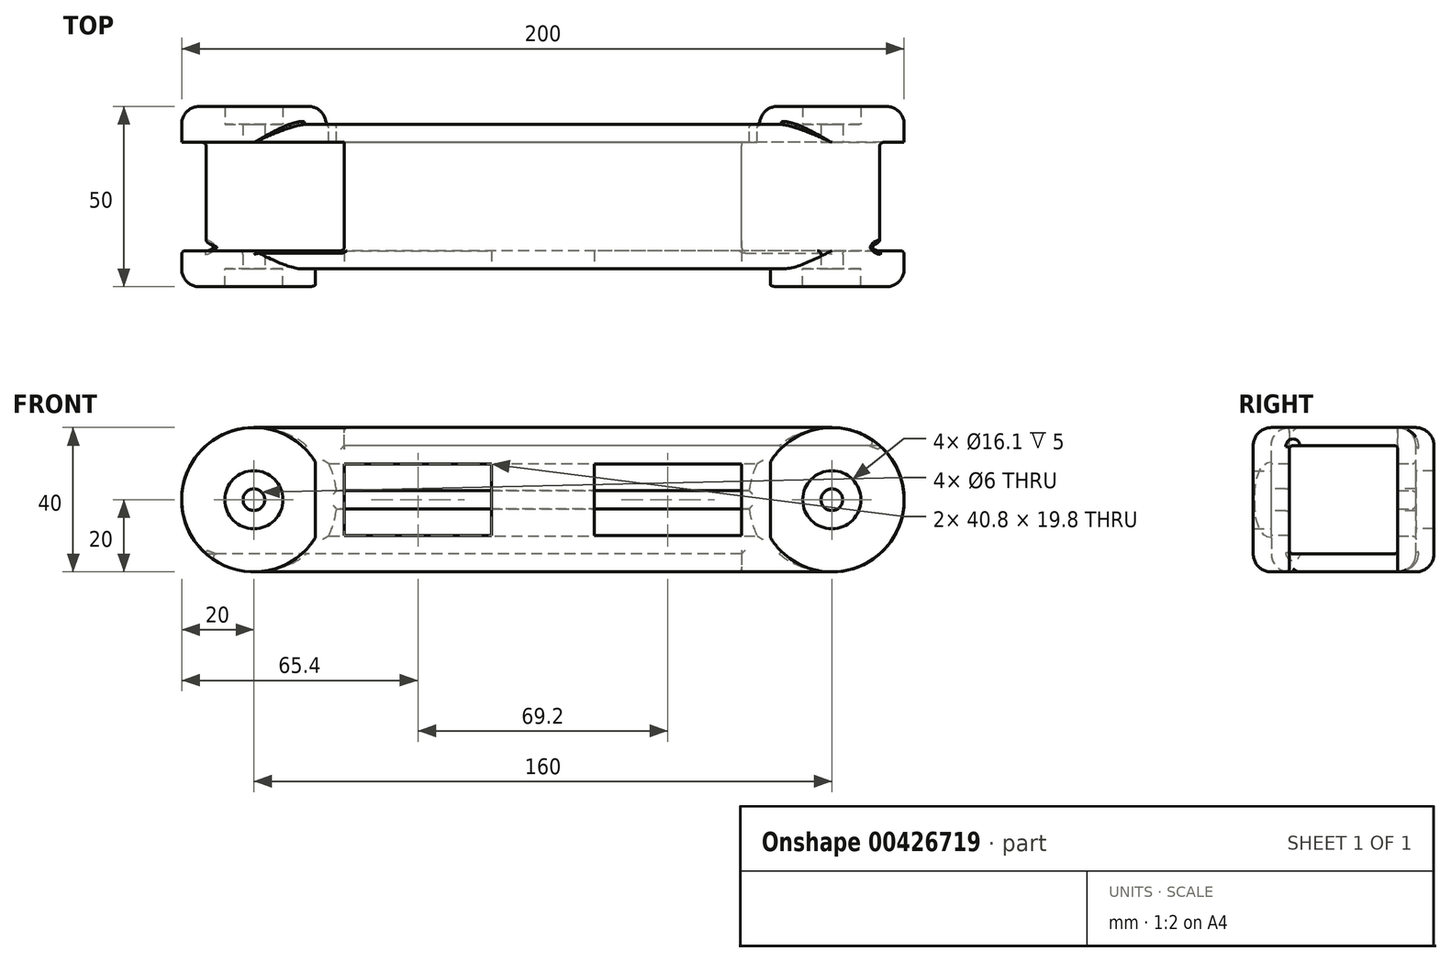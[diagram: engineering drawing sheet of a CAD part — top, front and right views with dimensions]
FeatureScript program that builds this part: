
annotation { "Feature Type Name" : "Feature", "Feature Type Description" : "" }
export const myFeature = defineFeature(function(context is Context, id is Id, definition is map)
    precondition{}
    {
        {
            var Q0;
            Q0=qCreatedBy(makeId("Right.planeOp"),FACE);
            var sketch = newSketch(context, id + "F0", { "sketchPlane" : qUnion([Q0])});
            skLineSegment(sketch, "E0.bottom", {"start": v(-20, -20) * mm, "end": v(20, -20) * mm});
            skLineSegment(sketch, "E0.top", {"start": v(-20, 20) * mm, "end": v(20, 20) * mm});
            skLineSegment(sketch, "E0.left", {"start": v(-20, -20) * mm, "end": v(-20, 20) * mm});
            skLineSegment(sketch, "E0.right", {"start": v(20, -20) * mm, "end": v(20, 20) * mm});
            skPoint(sketch, "E0.middle", {"position": v(0, 0) * mm});
            skLineSegment(sketch, "E1.bottom", {"start": v(-15, -15) * mm, "end": v(15, -15) * mm});
            skLineSegment(sketch, "E1.top", {"start": v(-15, 15) * mm, "end": v(15, 15) * mm});
            skLineSegment(sketch, "E1.left", {"start": v(-15, -15) * mm, "end": v(-15, 15) * mm});
            skLineSegment(sketch, "E1.right", {"start": v(15, -15) * mm, "end": v(15, 15) * mm});
            skSolve(sketch);
        }
        {
            var Q0;
            Q0=makeQuery(id+"F0.imprint","IMPRINT",FACE,{"disambiguationData":[TD([[makeQuery(id+"F0.imprint","IMPRINT",EDGE,{"derivedFrom":sQuery(id+"F0.wireOp",EDGE,"E0.bottom")}),1.0]])]});
            extrude(context, id + "F1", {"entities" : qUnion([Q0]), "depth" : 200 * mm});
        }
        {
            var Q0;
            Q0=makeQuery(id+"F1.opExtrude","SWEPT_FACE",FACE,{"disambiguationData":[OSD([sQuery(id+"F0.wireOp",EDGE,"E0.right")])]});
            var sketch = newSketch(context, id + "F2", { "sketchPlane" : qUnion([Q0])});
            skLineSegment(sketch, "E2", {"start": v(-238.83, 0) * mm, "end": v(24.92, 0) * mm, "construction": true});
            skPoint(sketch, "E2.endSnap0", {"position": v(-200, 0) * mm});
            skCircle(sketch, "E3", {"center": v(-180, 0) * mm, "radius": 20 * mm});
            skCircle(sketch, "E4", {"center": v(-20, 0) * mm, "radius": 20 * mm});
            skSolve(sketch);
        }
        {
            var Q0;
            {var subQ0=sQuery(id+"F2.wireOp",EDGE,"E3");var subQ1=sQuery(id+"F0.wireOp",EDGE,"E0.right");var subQ2=makeQuery(id+"F1.opExtrude","CAP_EDGE",EDGE,{"disambiguationData":[OSD([subQ1])],"isStart":false});var subQ3=makeQuery(id+"F2.imprint","INTERSECT",VERTEX,{"derivedFrom":[subQ2,subQ0]});Q0=makeQuery(id+"F2.imprint","IMPRINT",FACE,{"disambiguationData":[TD([[makeQuery(id+"F2.imprint","IMPRINT",EDGE,{"disambiguationData":[TD([[subQ3,-1.0]])],"derivedFrom":subQ0}),-1.0]])]});}
            var Q1;
            {var subQ0=sQuery(id+"F2.wireOp",EDGE,"E3");var subQ1=sQuery(id+"F0.wireOp",EDGE,"E0.right");var subQ2=makeQuery(id+"F1.opExtrude","CAP_EDGE",EDGE,{"disambiguationData":[OSD([subQ1])],"isStart":false});var subQ3=makeQuery(id+"F2.imprint","INTERSECT",VERTEX,{"derivedFrom":[subQ2,subQ0]});Q1=makeQuery(id+"F2.imprint","IMPRINT",FACE,{"disambiguationData":[TD([[makeQuery(id+"F2.imprint","IMPRINT",EDGE,{"disambiguationData":[TD([[subQ3,1.0]])],"derivedFrom":subQ0}),-1.0]])]});}
            var Q2;
            {var subQ0=sQuery(id+"F2.wireOp",EDGE,"E4");var subQ1=sQuery(id+"F0.wireOp",EDGE,"E0.right");var subQ4=makeQuery(id+"F1.opExtrude","CAP_EDGE",EDGE,{"disambiguationData":[OSD([subQ1])],"isStart":true});var subQ5=makeQuery(id+"F2.imprint","INTERSECT",VERTEX,{"derivedFrom":[subQ4,subQ0]});Q2=makeQuery(id+"F2.imprint","IMPRINT",FACE,{"disambiguationData":[TD([[makeQuery(id+"F2.imprint","IMPRINT",EDGE,{"disambiguationData":[TD([[subQ5,-1.0]])],"derivedFrom":subQ0}),-1.0]])]});}
            var Q3;
            {var subQ0=sQuery(id+"F2.wireOp",EDGE,"E4");var subQ1=sQuery(id+"F0.wireOp",EDGE,"E0.right");var subQ2=makeQuery(id+"F1.opExtrude","CAP_EDGE",EDGE,{"disambiguationData":[OSD([subQ1])],"isStart":true});var subQ3=makeQuery(id+"F2.imprint","INTERSECT",VERTEX,{"derivedFrom":[subQ2,subQ0]});Q3=makeQuery(id+"F2.imprint","IMPRINT",FACE,{"disambiguationData":[TD([[makeQuery(id+"F2.imprint","IMPRINT",EDGE,{"disambiguationData":[TD([[subQ3,1.0]])],"derivedFrom":subQ0}),-1.0]])]});}
            extrude(context, id + "F3", {"entities" : qUnion([Q0, Q1, Q2, Q3]), "operationType" : NewBodyOperationType.REMOVE, "oppositeDirection" : true, "depth" : 40 * mm});
        }
        {
            var Q0;
            Q0=makeQuery(id+"F1.opExtrude","SWEPT_FACE",FACE,{"disambiguationData":[OSD([sQuery(id+"F0.wireOp",EDGE,"E0.right")])]});
            var sketch = newSketch(context, id + "F4", { "sketchPlane" : qUnion([Q0])});
            skLineSegment(sketch, "E5", {"start": v(-227.1, 0) * mm, "end": v(25.36, 0) * mm, "construction": true});
            skCircle(sketch, "E6", {"center": v(-180, 0) * mm, "radius": 20 * mm});
            skCircle(sketch, "E7", {"center": v(-20, 0) * mm, "radius": 20 * mm});
            skCircle(sketch, "E8", {"center": v(-20, 0) * mm, "radius": 8.05 * mm});
            skCircle(sketch, "E9", {"center": v(-180, 0) * mm, "radius": 8.05 * mm});
            skSolve(sketch);
        }
        {
            var Q0;
            Q0 = qSketchRegion(id + "F4", true);
            extrude(context, id + "F5", {"entities" : qUnion([Q0]), "operationType" : NewBodyOperationType.ADD, "depth" : 5 * mm});
        }
        {
            var Q0;
            Q0=makeQuery(id+"F1.opExtrude","SWEPT_FACE",FACE,{"disambiguationData":[OSD([sQuery(id+"F0.wireOp",EDGE,"E0.left")])]});
            var sketch = newSketch(context, id + "F6", { "sketchPlane" : qUnion([Q0])});
            skLineSegment(sketch, "E10", {"start": v(-11.87, 0) * mm, "end": v(168.62, 0) * mm, "construction": true});
            skCircle(sketch, "E11", {"center": v(20, 0) * mm, "radius": 20 * mm});
            skCircle(sketch, "E12", {"center": v(20, 0) * mm, "radius": 8.05 * mm});
            skCircle(sketch, "E13", {"center": v(180, 0) * mm, "radius": 20 * mm});
            skCircle(sketch, "E14", {"center": v(180, 0) * mm, "radius": 8.05 * mm});
            skSolve(sketch);
        }
        {
            var Q0;
            Q0 = qSketchRegion(id + "F6", true);
            extrude(context, id + "F7", {"entities" : qUnion([Q0]), "operationType" : NewBodyOperationType.ADD, "depth" : 5 * mm});
        }
        {
            var Q0;
            {var subQ3=sQuery(id+"F0.wireOp",EDGE,"E0.bottom");Q0=makeQuery(id+"F7.boolean.opBoolean","SPLIT",FACE,{"disambiguationData":[TD([makeQuery(id+"F1.opExtrude","SWEPT_FACE",FACE,{"disambiguationData":[OSD([subQ3])]})])],"derivedFrom":makeQuery(id+"F1.opExtrude","SWEPT_FACE",FACE,{"disambiguationData":[OSD([sQuery(id+"F0.wireOp",EDGE,"E0.left")])]})});}
            var sketch = newSketch(context, id + "F8", { "sketchPlane" : qUnion([Q0])});
            skCircle(sketch, "E15", {"center": v(20, 0) * mm, "radius": 3 * mm});
            skCircle(sketch, "E16", {"center": v(180, 0) * mm, "radius": 3 * mm});
            skSolve(sketch);
        }
        {
            var Q0;
            Q0 = qSketchRegion(id + "F8", true);
            extrude(context, id + "F9", {"entities" : qUnion([Q0]), "operationType" : NewBodyOperationType.REMOVE, "oppositeDirection" : true, "depth" : 40 * mm});
        }
        {
            var Q0;
            Q0=makeQuery(id+"F1.opExtrude","SWEPT_FACE",FACE,{"disambiguationData":[OSD([sQuery(id+"F0.wireOp",EDGE,"E0.bottom")])]});
            var sketch = newSketch(context, id + "F10", { "sketchPlane" : qUnion([Q0])});
            skLineSegment(sketch, "E17.bottom", {"start": v(205, 15) * mm, "end": v(155, 15) * mm});
            skLineSegment(sketch, "E17.top", {"start": v(205, -15) * mm, "end": v(155, -15) * mm});
            skLineSegment(sketch, "E17.left", {"start": v(205, 15) * mm, "end": v(205, -15) * mm});
            skLineSegment(sketch, "E17.right", {"start": v(155, 15) * mm, "end": v(155, -15) * mm});
            skPoint(sketch, "E17.middle", {"position": v(180, 0) * mm});
            skSolve(sketch);
        }
        {
            var Q0;
            Q0 = qSketchRegion(id + "F10", true);
            extrude(context, id + "F11", {"entities" : qUnion([Q0]), "operationType" : NewBodyOperationType.REMOVE, "oppositeDirection" : true, "depth" : 5 * mm});
        }
        {
            var Q0;
            Q0=makeQuery(id+"F1.opExtrude","SWEPT_FACE",FACE,{"disambiguationData":[OSD([sQuery(id+"F0.wireOp",EDGE,"E0.top")])]});
            var sketch = newSketch(context, id + "F12", { "sketchPlane" : qUnion([Q0])});
            skLineSegment(sketch, "E18.bottom", {"start": v(0, 15) * mm, "end": v(40, 15) * mm});
            skLineSegment(sketch, "E18.top", {"start": v(0, -15) * mm, "end": v(40, -15) * mm});
            skLineSegment(sketch, "E18.left", {"start": v(0, 15) * mm, "end": v(0, -15) * mm});
            skPoint(sketch, "E18.middle", {"position": v(20, 0) * mm});
            skLineSegment(sketch, "E19.bottom", {"start": v(40, 15) * mm, "end": v(45, 15) * mm});
            skLineSegment(sketch, "E19.top", {"start": v(40, -15) * mm, "end": v(45, -15) * mm});
            skLineSegment(sketch, "E19.right", {"start": v(45, 15) * mm, "end": v(45, -15) * mm});
            skSolve(sketch);
        }
        {
            var Q0;
            Q0 = qSketchRegion(id + "F12", true);
            extrude(context, id + "F13", {"entities" : qUnion([Q0]), "operationType" : NewBodyOperationType.REMOVE, "oppositeDirection" : true, "depth" : 5 * mm});
        }
        {
            var Q0;
            Q0=makeQuery(id+"F13.boolean.opBoolean","MERGE",FACE,{"derivedFrom":[makeQuery(id+"F11.boolean.opBoolean","MERGE",FACE,{"derivedFrom":[makeQuery(id+"F1.opExtrude","SWEPT_FACE",FACE,{"disambiguationData":[OSD([sQuery(id+"F0.wireOp",EDGE,"E1.left")])]}),makeQuery(id+"F11.opExtrude","SWEPT_FACE",FACE,{"disambiguationData":[OSD([sQuery(id+"F10.wireOp",EDGE,"E17.bottom")])]})]}),makeQuery(id+"F13.opExtrude","SWEPT_FACE",FACE,{"disambiguationData":[OSD([sQuery(id+"F12.wireOp",EDGE,"E18.top")])]})]});
            var Q1;
            Q1=makeQuery(id+"F1.opExtrude","SWEPT_EDGE",EDGE,{"disambiguationData":[OSD([sQuery(id+"F0.wireOp",EDGE,"E1.bottom"),sQuery(id+"F0.wireOp",EDGE,"E1.right")])]});
            var Q2;
            Q2=makeQuery(id+"F1.opExtrude","SWEPT_EDGE",EDGE,{"disambiguationData":[OSD([sQuery(id+"F0.wireOp",EDGE,"E1.top"),sQuery(id+"F0.wireOp",EDGE,"E1.left")])]});
            var Q3;
            Q3=makeQuery(id+"F1.opExtrude","SWEPT_EDGE",EDGE,{"disambiguationData":[OSD([sQuery(id+"F0.wireOp",EDGE,"E1.top"),sQuery(id+"F0.wireOp",EDGE,"E1.right")])]});
            fillet(context, id + "F14", {"entities" : qUnion([Q0, Q1, Q2, Q3]), "radius" : 1 * mm, "tangentPropagation" : true, "allowEdgeOverflow" : false});
        }
        {
            var Q0;
            {var subQ3=sQuery(id+"F0.wireOp",EDGE,"E0.bottom");Q0=makeQuery(id+"F7.boolean.opBoolean","SPLIT",FACE,{"disambiguationData":[TD([makeQuery(id+"F1.opExtrude","SWEPT_FACE",FACE,{"disambiguationData":[OSD([subQ3])]})])],"derivedFrom":makeQuery(id+"F1.opExtrude","SWEPT_FACE",FACE,{"disambiguationData":[OSD([sQuery(id+"F0.wireOp",EDGE,"E0.left")])]})});}
            var sketch = newSketch(context, id + "F15", { "sketchPlane" : qUnion([Q0])});
            skLineSegment(sketch, "E20", {"start": v(219.32, 0) * mm, "end": v(-21.86, 0) * mm, "construction": true});
            skPoint(sketch, "E20.endSnap0", {"position": v(160, 0) * mm});
            skLineSegment(sketch, "E21.bottom", {"start": v(155, -9.9) * mm, "end": v(114.2, -9.9) * mm});
            skLineSegment(sketch, "E21.top", {"start": v(155, 9.9) * mm, "end": v(114.2, 9.9) * mm});
            skLineSegment(sketch, "E21.left", {"start": v(155, -9.9) * mm, "end": v(155, 9.9) * mm});
            skLineSegment(sketch, "E21.right", {"start": v(114.2, -9.9) * mm, "end": v(114.2, 9.9) * mm});
            skPoint(sketch, "E21.middle", {"position": v(134.6, 0) * mm});
            skLineSegment(sketch, "E22.bottom", {"start": v(45, -9.9) * mm, "end": v(85.8, -9.9) * mm});
            skLineSegment(sketch, "E22.top", {"start": v(45, 9.9) * mm, "end": v(85.8, 9.9) * mm});
            skLineSegment(sketch, "E22.left", {"start": v(45, -9.9) * mm, "end": v(45, 9.9) * mm});
            skLineSegment(sketch, "E22.right", {"start": v(85.8, -9.9) * mm, "end": v(85.8, 9.9) * mm});
            skPoint(sketch, "E22.middle", {"position": v(65.4, 0) * mm});
            skSolve(sketch);
        }
        {
            var Q0;
            Q0 = qSketchRegion(id + "F15", true);
            extrude(context, id + "F16", {"entities" : qUnion([Q0]), "operationType" : NewBodyOperationType.REMOVE, "oppositeDirection" : true, "depth" : 5 * mm});
        }
        {
            var Q0;
            Q0=makeQuery(id+"F7.opExtrude","CAP_FACE",FACE,{"disambiguationData":[OSD([sQuery(id+"F6.wireOp",EDGE,"E13"),sQuery(id+"F6.wireOp",EDGE,"E14")])],"isStart":false});
            var sketch = newSketch(context, id + "F17", { "sketchPlane" : qUnion([Q0])});
            skLineSegment(sketch, "E23", {"start": v(208.93, 0) * mm, "end": v(133.4, 0) * mm, "construction": true});
            skLineSegment(sketch, "E24.bottom", {"start": v(163, -12.5) * mm, "end": v(157, -12.5) * mm});
            skLineSegment(sketch, "E24.top", {"start": v(163, 12.5) * mm, "end": v(157, 12.5) * mm});
            skLineSegment(sketch, "E24.left", {"start": v(163, -12.5) * mm, "end": v(163, 12.5) * mm});
            skLineSegment(sketch, "E24.right", {"start": v(157, -12.5) * mm, "end": v(157, 12.5) * mm});
            skPoint(sketch, "E24.middle", {"position": v(160, 0) * mm});
            skSolve(sketch);
        }
        {
            var Q0;
            Q0 = qSketchRegion(id + "F17", true);
            extrude(context, id + "F18", {"entities" : qUnion([Q0]), "operationType" : NewBodyOperationType.REMOVE, "oppositeDirection" : true, "depth" : 5 * mm});
        }
        {
            var Q0;
            {var subQ3=sQuery(id+"F0.wireOp",EDGE,"E0.bottom");Q0=makeQuery(id+"F18.boolean.opBoolean","MERGE",FACE,{"derivedFrom":[makeQuery(id+"F7.boolean.opBoolean","SPLIT",FACE,{"disambiguationData":[TD([makeQuery(id+"F1.opExtrude","SWEPT_FACE",FACE,{"disambiguationData":[OSD([subQ3])]})])],"derivedFrom":makeQuery(id+"F1.opExtrude","SWEPT_FACE",FACE,{"disambiguationData":[OSD([sQuery(id+"F0.wireOp",EDGE,"E0.left")])]})}),makeQuery(id+"F18.opExtrude","CAP_FACE",FACE,{"disambiguationData":[OSD([sQuery(id+"F17.wireOp",EDGE,"E24.bottom"),sQuery(id+"F17.wireOp",EDGE,"E24.top"),sQuery(id+"F17.wireOp",EDGE,"E24.left"),sQuery(id+"F17.wireOp",EDGE,"E24.right")])],"isStart":false})]});}
            var sketch = newSketch(context, id + "F19", { "sketchPlane" : qUnion([Q0])});
            skLineSegment(sketch, "E25.bottom", {"start": v(37, -12.5) * mm, "end": v(53, -12.5) * mm});
            skLineSegment(sketch, "E25.top", {"start": v(37, 12.5) * mm, "end": v(53, 12.5) * mm});
            skLineSegment(sketch, "E25.left", {"start": v(37, -12.5) * mm, "end": v(37, 12.5) * mm});
            skLineSegment(sketch, "E25.right", {"start": v(53, -12.5) * mm, "end": v(53, 12.5) * mm});
            skPoint(sketch, "E25.middle", {"position": v(45, 0) * mm});
            skSolve(sketch);
        }
        {
            var Q0;
            Q0 = qSketchRegion(id + "F19", true);
            extrude(context, id + "F20", {"entities" : qUnion([Q0]), "operationType" : NewBodyOperationType.REMOVE, "depth" : 5 * mm});
        }
        {
            var Q0;
            Q0=makeQuery(id+"F7.opExtrude","CAP_EDGE",EDGE,{"disambiguationData":[OSD([sQuery(id+"F6.wireOp",EDGE,"E13")])],"isStart":false});
            var Q1;
            Q1=makeQuery(id+"F7.opExtrude","CAP_EDGE",EDGE,{"disambiguationData":[OSD([sQuery(id+"F6.wireOp",EDGE,"E11")])],"isStart":false});
            var Q2;
            Q2=makeQuery(id+"F1.opExtrude","SWEPT_EDGE",EDGE,{"disambiguationData":[OSD([sQuery(id+"F0.wireOp",EDGE,"E0.top"),sQuery(id+"F0.wireOp",EDGE,"E0.left")])]});
            var Q3;
            Q3=makeQuery(id+"F1.opExtrude","SWEPT_EDGE",EDGE,{"disambiguationData":[OSD([sQuery(id+"F0.wireOp",EDGE,"E0.bottom"),sQuery(id+"F0.wireOp",EDGE,"E0.left")])]});
            fillet(context, id + "F21", {"entities" : qUnion([Q0, Q1, Q2, Q3]), "radius" : 5 * mm, "tangentPropagation" : true, "allowEdgeOverflow" : false});
        }
        {
            var Q0;
            Q0=makeQuery(id+"F5.opExtrude","CAP_EDGE",EDGE,{"disambiguationData":[OSD([sQuery(id+"F4.wireOp",EDGE,"E7")])],"isStart":false});
            var Q1;
            Q1=makeQuery(id+"F5.opExtrude","CAP_EDGE",EDGE,{"disambiguationData":[OSD([sQuery(id+"F4.wireOp",EDGE,"E6")])],"isStart":false});
            var Q2;
            Q2=makeQuery(id+"F1.opExtrude","SWEPT_EDGE",EDGE,{"disambiguationData":[OSD([sQuery(id+"F0.wireOp",EDGE,"E0.bottom"),sQuery(id+"F0.wireOp",EDGE,"E0.right")])]});
            var Q3;
            Q3=makeQuery(id+"F1.opExtrude","SWEPT_EDGE",EDGE,{"disambiguationData":[OSD([sQuery(id+"F0.wireOp",EDGE,"E0.top"),sQuery(id+"F0.wireOp",EDGE,"E0.right")])]});
            fillet(context, id + "F22", {"entities" : qUnion([Q0, Q1, Q2, Q3]), "radius" : 5 * mm, "tangentPropagation" : true, "allowEdgeOverflow" : false});
        }
        {
            var Q0;
            {var subQ1=sQuery(id+"F0.wireOp",EDGE,"E0.right");var subQ3=sQuery(id+"F0.wireOp",EDGE,"E0.bottom");Q0=makeQuery(id+"F5.boolean.opBoolean","SPLIT",FACE,{"disambiguationData":[TD([makeQuery(id+"F1.opExtrude","SWEPT_FACE",FACE,{"disambiguationData":[OSD([subQ3])]})])],"derivedFrom":makeQuery(id+"F1.opExtrude","SWEPT_FACE",FACE,{"disambiguationData":[OSD([subQ1])]})});}
            var sketch = newSketch(context, id + "F23", { "sketchPlane" : qUnion([Q0])});
            skLineSegment(sketch, "E26", {"start": v(-224.05, 0) * mm, "end": v(21.88, 0) * mm, "construction": true});
            skLineSegment(sketch, "E27", {"start": v(-160, 33.4) * mm, "end": v(-160, -38.78) * mm, "construction": true});
            skLineSegment(sketch, "E28", {"start": v(-40, 38.7) * mm, "end": v(-40, -38.78) * mm, "construction": true});
            skLineSegment(sketch, "E29", {"start": v(-160, 10) * mm, "end": v(-40.71, 10) * mm});
            skLineSegment(sketch, "E30", {"start": v(-160, -10) * mm, "end": v(-40, -10) * mm});
            skArc(sketch, "E31", {"start": v(-157.14, 2.5) * mm, "mid": v(-157.9, 6.34) * mm, "end": v(-159.29, 10) * mm});
            skArc(sketch, "E32", {"start": v(-42.86, -2.5) * mm, "mid": v(-42.1, -6.34) * mm, "end": v(-40.71, -10) * mm});
            skLineSegment(sketch, "E33", {"start": v(-157.14, 2.5) * mm, "end": v(-42.86, 2.5) * mm});
            skLineSegment(sketch, "E34", {"start": v(-157.14, -2.5) * mm, "end": v(-42.86, -2.5) * mm});
            skPoint(sketch, "E35", {"position": v(-40.71, 10) * mm});
            skPoint(sketch, "E36", {"position": v(-42.86, 2.5) * mm});
            skPoint(sketch, "E37", {"position": v(-42.86, -2.5) * mm});
            skPoint(sketch, "E38", {"position": v(-40.71, -10) * mm});
            skPoint(sketch, "E39", {"position": v(-159.29, 10) * mm});
            skPoint(sketch, "E40", {"position": v(-157.14, 2.5) * mm});
            skPoint(sketch, "E41", {"position": v(-157.14, -2.5) * mm});
            skPoint(sketch, "E42", {"position": v(-159.29, -10) * mm});
            skArc(sketch, "E43.trimOffspring", {"start": v(-40.71, 10) * mm, "mid": v(-42.1, 6.34) * mm, "end": v(-42.86, 2.5) * mm});
            skArc(sketch, "E44.trimOffspring", {"start": v(-159.29, -10) * mm, "mid": v(-157.9, -6.34) * mm, "end": v(-157.14, -2.5) * mm});
            skSolve(sketch);
        }
        {
            var Q0;
            {var subQ2=sQuery(id+"F23.wireOp",EDGE,"E31");Q0=makeQuery(id+"F23.imprint","IMPRINT",FACE,{"disambiguationData":[TD([[makeQuery(id+"F23.imprint","IMPRINT",EDGE,{"derivedFrom":subQ2}),-1.0]])]});}
            var Q1;
            {var subQ0=sQuery(id+"F23.wireOp",EDGE,"E32");Q1=makeQuery(id+"F23.imprint","IMPRINT",FACE,{"disambiguationData":[TD([[makeQuery(id+"F23.imprint","IMPRINT",EDGE,{"derivedFrom":subQ0}),-1.0]])]});}
            extrude(context, id + "F24", {"entities" : qUnion([Q0, Q1]), "operationType" : NewBodyOperationType.REMOVE, "oppositeDirection" : true, "depth" : 10 * mm});
        }
        {
            var Q0;
            Q0=makeQuery(id+"F24.boolean.opBoolean","COPY",EDGE,{"derivedFrom":makeQuery(id+"F24.opExtrude","CAP_EDGE",EDGE,{"disambiguationData":[OSD([sQuery(id+"F23.wireOp",EDGE,"E29")])],"isStart":true})});
            var Q1;
            Q1=makeQuery(id+"F24.boolean.opBoolean","COPY",EDGE,{"derivedFrom":makeQuery(id+"F24.opExtrude","CAP_EDGE",EDGE,{"disambiguationData":[OSD([sQuery(id+"F23.wireOp",EDGE,"E31")])],"isStart":true})});
            var Q2;
            Q2=makeQuery(id+"F24.boolean.opBoolean","COPY",EDGE,{"derivedFrom":makeQuery(id+"F24.opExtrude","CAP_EDGE",EDGE,{"disambiguationData":[OSD([sQuery(id+"F23.wireOp",EDGE,"E44.trimOffspring")])],"isStart":true})});
            var Q3;
            Q3=makeQuery(id+"F24.boolean.opBoolean","COPY",EDGE,{"derivedFrom":makeQuery(id+"F24.opExtrude","CAP_EDGE",EDGE,{"disambiguationData":[OSD([sQuery(id+"F23.wireOp",EDGE,"E34")])],"isStart":true})});
            var Q4;
            Q4=makeQuery(id+"F24.boolean.opBoolean","COPY",EDGE,{"derivedFrom":makeQuery(id+"F24.opExtrude","CAP_EDGE",EDGE,{"disambiguationData":[OSD([sQuery(id+"F23.wireOp",EDGE,"E30")])],"isStart":true})});
            var Q5;
            Q5=makeQuery(id+"F24.boolean.opBoolean","COPY",EDGE,{"derivedFrom":makeQuery(id+"F24.opExtrude","CAP_EDGE",EDGE,{"disambiguationData":[OSD([sQuery(id+"F23.wireOp",EDGE,"E32")])],"isStart":true})});
            var Q6;
            Q6=makeQuery(id+"F24.boolean.opBoolean","COPY",EDGE,{"derivedFrom":makeQuery(id+"F24.opExtrude","CAP_EDGE",EDGE,{"disambiguationData":[OSD([sQuery(id+"F23.wireOp",EDGE,"E43.trimOffspring")])],"isStart":true})});
            var Q7;
            Q7=makeQuery(id+"F24.boolean.opBoolean","COPY",EDGE,{"derivedFrom":makeQuery(id+"F24.opExtrude","CAP_EDGE",EDGE,{"disambiguationData":[OSD([sQuery(id+"F23.wireOp",EDGE,"E33")])],"isStart":true})});
            var Q8;
            {var subQ1=sQuery(id+"F0.wireOp",EDGE,"E0.right");var subQ3=sQuery(id+"F0.wireOp",EDGE,"E0.bottom");Q8=makeQuery(id+"F5.boolean.opBoolean","SPLIT",FACE,{"disambiguationData":[TD([makeQuery(id+"F1.opExtrude","SWEPT_FACE",FACE,{"disambiguationData":[OSD([subQ3])]})])],"derivedFrom":makeQuery(id+"F1.opExtrude","SWEPT_FACE",FACE,{"disambiguationData":[OSD([subQ1])]})});}
            fillet(context, id + "F25", {"entities" : qUnion([Q0, Q1, Q2, Q3, Q4, Q5, Q6, Q7, Q8]), "radius" : 1 * mm, "tangentPropagation" : true, "allowEdgeOverflow" : false});
        }
    });
